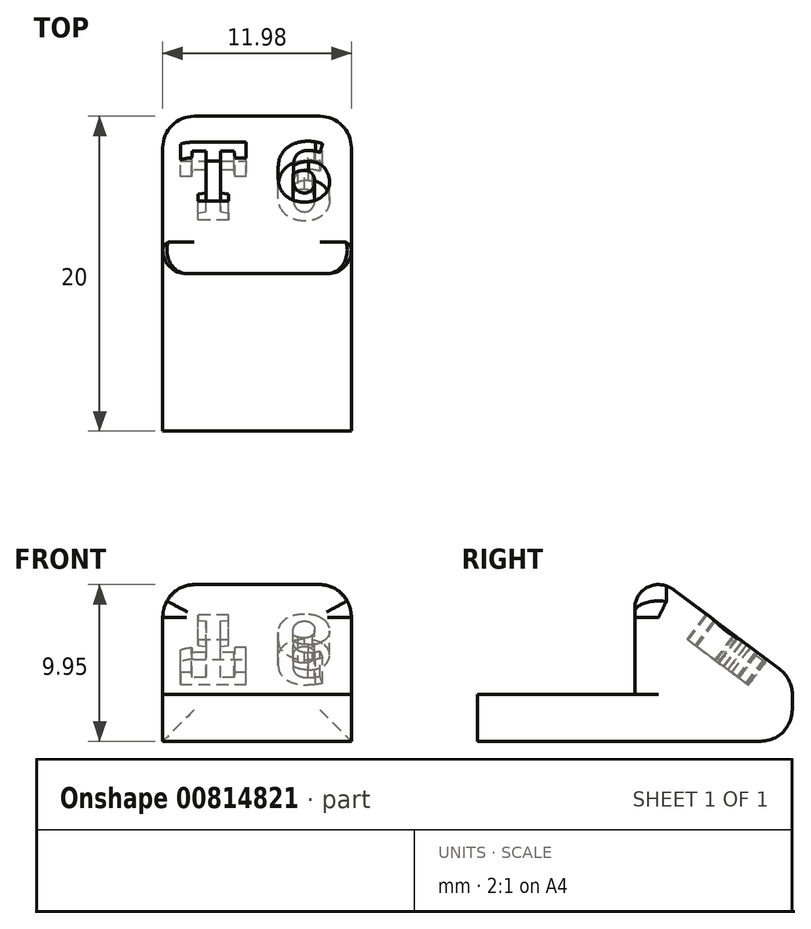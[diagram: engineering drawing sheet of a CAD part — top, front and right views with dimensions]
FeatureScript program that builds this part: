
annotation { "Feature Type Name" : "Feature", "Feature Type Description" : "" }
export const myFeature = defineFeature(function(context is Context, id is Id, definition is map)
    precondition{}
    {
        {
            var Q0;
            Q0=qCreatedBy(makeId("Top.planeOp"),FACE);
            var sketch = newSketch(context, id + "F0", { "sketchPlane" : qUnion([Q0])});
            skLineSegment(sketch, "E0.bottom", {"start": v(6, 10) * mm, "end": v(-5.99, 10) * mm});
            skLineSegment(sketch, "E0.top", {"start": v(6, -10) * mm, "end": v(-5.99, -10) * mm});
            skLineSegment(sketch, "E0.left", {"start": v(6, 10) * mm, "end": v(6, -10) * mm});
            skLineSegment(sketch, "E0.right", {"start": v(-5.99, 10) * mm, "end": v(-5.99, -10) * mm});
            skPoint(sketch, "E0.middle", {"position": v(0, 0) * mm});
            skSolve(sketch);
        }
        {
            var Q0;
            Q0=qSketchRegion(id+"F0",true);
            extrude(context, id + "F1", {"entities" : qUnion([Q0]), "depth" : 2.98 * mm, "offsetDistance" : 25 * mm});
        }
        {
            var Q0;
            Q0=makeQuery(id+"F1.opExtrude","CAP_FACE",FACE,{"disambiguationData":[OSD([sQuery(id+"F0.wireOp",EDGE,"E0.bottom"),sQuery(id+"F0.wireOp",EDGE,"E0.top"),sQuery(id+"F0.wireOp",EDGE,"E0.left"),sQuery(id+"F0.wireOp",EDGE,"E0.right")])],"isStart":false});
            var sketch = newSketch(context, id + "F2", { "sketchPlane" : qUnion([Q0])});
            skLineSegment(sketch, "E1.bottom", {"start": v(-5.99, 10) * mm, "end": v(6, 10) * mm});
            skLineSegment(sketch, "E1.top", {"start": v(-5.99, 0) * mm, "end": v(6, 0) * mm});
            skLineSegment(sketch, "E1.left", {"start": v(-5.99, 10) * mm, "end": v(-5.99, 0) * mm});
            skLineSegment(sketch, "E1.right", {"start": v(6, 10) * mm, "end": v(6, 0) * mm});
            skSolve(sketch);
        }
        {
            var Q0;
            Q0=makeQuery(id+"F2.imprint","IMPRINT",FACE,{"disambiguationData":[TD([[makeQuery(id+"F2.imprint","IMPRINT",EDGE,{"derivedFrom":sQuery(id+"F2.wireOp",EDGE,"E1.bottom")}),1.0]])]});
            extrude(context, id + "F3", {"entities" : qUnion([Q0]), "operationType" : NewBodyOperationType.ADD, "depth" : 7 * mm, "offsetDistance" : 25 * mm});
        }
        {
            var Q0;
            Q0=makeQuery(id+"F3.opExtrude","CAP_EDGE",EDGE,{"disambiguationData":[OSD([sQuery(id+"F2.wireOp",EDGE,"E1.bottom")])],"isStart":false});
            chamfer(context, id + "F4", {"entities" : qUnion([Q0]), "chamferType" : ChamferType.TWO_OFFSETS, "width1" : 8 * mm, "oppositeDirection" : false, "width2" : 6 * mm, "tangentPropagation" : true});
        }
        {
            var Q0;
            Q0=makeQuery(id+"F4.opChamfer","BLEND_FACE",FACE,{"disambiguationData":[OSD([sQuery(id+"F2.wireOp",EDGE,"E1.bottom")])]});
            var sketch = newSketch(context, id + "F5", { "sketchPlane" : qUnion([Q0])});
            skText(sketch, "E2", { "text": "T 6", "fontName": "RobotoSlab-Bold.ttf"});
            const initialGuessF5  = {"E2": [-0.005, -0.00113, 1, 0, 0.00475]};
            skSetInitialGuess(sketch, initialGuessF5);
            skSolve(sketch);
        }
        {
            var Q0;
            Q0 = qSketchRegion(id + "F5", true);
            extrude(context, id + "F6", {"entities" : qUnion([Q0]), "operationType" : NewBodyOperationType.REMOVE, "oppositeDirection" : true, "depth" : 2 * mm, "offsetDistance" : 25 * mm});
        }
        {
            var Q0;
            Q0=makeQuery(id+"F3.boolean.opBoolean","MERGE",FACE,{"derivedFrom":[makeQuery(id+"F1.opExtrude","SWEPT_FACE",FACE,{"disambiguationData":[OSD([sQuery(id+"F0.wireOp",EDGE,"E0.bottom")])]}),makeQuery(id+"F3.opExtrude","SWEPT_FACE",FACE,{"disambiguationData":[OSD([sQuery(id+"F2.wireOp",EDGE,"E1.bottom")])]})]});
            var Q1;
            Q1=makeQuery(id+"F4.opChamfer","BLEND_EDGE",EDGE,{"blendedFrom":[makeQuery(id+"F3.opExtrude","CAP_EDGE",EDGE,{"disambiguationData":[OSD([sQuery(id+"F2.wireOp",EDGE,"E1.bottom")])],"isStart":false}),makeQuery(id+"F3.boolean.opBoolean","MERGE",FACE,{"derivedFrom":[makeQuery(id+"F1.opExtrude","SWEPT_FACE",FACE,{"disambiguationData":[OSD([sQuery(id+"F0.wireOp",EDGE,"E0.left")])]}),makeQuery(id+"F3.opExtrude","SWEPT_FACE",FACE,{"disambiguationData":[OSD([sQuery(id+"F2.wireOp",EDGE,"E1.right")])]})]})],"blendedInto":[makeQuery(id+"F3.boolean.opBoolean","MERGE",FACE,{"derivedFrom":[makeQuery(id+"F1.opExtrude","SWEPT_FACE",FACE,{"disambiguationData":[OSD([sQuery(id+"F0.wireOp",EDGE,"E0.left")])]}),makeQuery(id+"F3.opExtrude","SWEPT_FACE",FACE,{"disambiguationData":[OSD([sQuery(id+"F2.wireOp",EDGE,"E1.right")])]})]})]});
            var Q2;
            Q2=makeQuery(id+"F4.opChamfer","BLEND_EDGE",EDGE,{"blendedFrom":[makeQuery(id+"F3.opExtrude","CAP_EDGE",EDGE,{"disambiguationData":[OSD([sQuery(id+"F2.wireOp",EDGE,"E1.bottom")])],"isStart":false}),makeQuery(id+"F3.boolean.opBoolean","MERGE",FACE,{"derivedFrom":[makeQuery(id+"F1.opExtrude","SWEPT_FACE",FACE,{"disambiguationData":[OSD([sQuery(id+"F0.wireOp",EDGE,"E0.right")])]}),makeQuery(id+"F3.opExtrude","SWEPT_FACE",FACE,{"disambiguationData":[OSD([sQuery(id+"F2.wireOp",EDGE,"E1.left")])]})]})],"blendedInto":[makeQuery(id+"F3.boolean.opBoolean","MERGE",FACE,{"derivedFrom":[makeQuery(id+"F1.opExtrude","SWEPT_FACE",FACE,{"disambiguationData":[OSD([sQuery(id+"F0.wireOp",EDGE,"E0.right")])]}),makeQuery(id+"F3.opExtrude","SWEPT_FACE",FACE,{"disambiguationData":[OSD([sQuery(id+"F2.wireOp",EDGE,"E1.left")])]})]})]});
            var Q3;
            Q3=makeQuery(id+"F3.opExtrude","CAP_EDGE",EDGE,{"disambiguationData":[OSD([sQuery(id+"F2.wireOp",EDGE,"E1.right")])],"isStart":false});
            var Q4;
            Q4=makeQuery(id+"F3.opExtrude","CAP_EDGE",EDGE,{"disambiguationData":[OSD([sQuery(id+"F2.wireOp",EDGE,"E1.left")])],"isStart":false});
            var Q5;
            {var subQ0=sQuery(id+"F2.wireOp",EDGE,"E1.bottom");Q5=makeQuery(id+"F4.opChamfer","BLEND_EDGE",EDGE,{"blendedFrom":[makeQuery(id+"F3.opExtrude","CAP_EDGE",EDGE,{"disambiguationData":[OSD([subQ0])],"isStart":false}),makeQuery(id+"F3.opExtrude","CAP_FACE",FACE,{"disambiguationData":[OSD([subQ0,sQuery(id+"F2.wireOp",EDGE,"E1.top"),sQuery(id+"F2.wireOp",EDGE,"E1.left"),sQuery(id+"F2.wireOp",EDGE,"E1.right")])],"isStart":false})],"blendedInto":[makeQuery(id+"F3.opExtrude","CAP_FACE",FACE,{"disambiguationData":[OSD([subQ0,sQuery(id+"F2.wireOp",EDGE,"E1.top"),sQuery(id+"F2.wireOp",EDGE,"E1.left"),sQuery(id+"F2.wireOp",EDGE,"E1.right")])],"isStart":false})]});}
            fillet(context, id + "F7", {"entities" : qUnion([Q0, Q1, Q2, Q3, Q4, Q5]), "radius" : 2 * mm, "tangentPropagation" : true, "allowEdgeOverflow" : false});
        }
        {
            var Q0;
            Q0=makeQuery(id+"F3.opExtrude","CAP_EDGE",EDGE,{"disambiguationData":[OSD([sQuery(id+"F2.wireOp",EDGE,"E1.top")])],"isStart":false});
            fillet(context, id + "F8", {"entities" : qUnion([Q0]), "radius" : 1.5 * mm, "tangentPropagation" : true, "allowEdgeOverflow" : false});
        }
    });
